# Revit family: Messblende 4000
name_source: partatom
category: Rohrzubehör
units: mm (PartAtom-declared; Revit-internal decimal feet)

## family parameters
Arbeitsebenenbasiert = Nein
Beim Laden mit Abzugskörper schneiden = Nein
Bemaßung runder Anschluss = Durchmesser verwenden
Gemeinsam genutzt = Nein
Immer vertikal = Ja
OmniClass-Nummer = 23.65.55.14
OmniClass-Titel = Valves for Liquid Services
Teiletyp = Unterbricht

## types (1)
- Messblende 4000
    Ausführung = Die Messblende aus entzinkungsbeständigem Messing besitzt zwei Messventile. Gemäß EN 10226 hat der Eingang ein Innengewinde Rp und der Ausgang ein Außengewinde R.
    Gehäuse = Messing, CC770S
    Hersteller = HERZ Armaturen Ges.m.b.H.
    Max. Betriebsdruck = 2000000.0 Pa
    Max. Betriebstemperatur (ab DN40) = 110 °C
    Max. Betriebstemperatur (bis DN32) = 130 °C
    Medium = Heizungswasserqualität nach ÖNORM H 5195 oder VDI-Richtline 2035.
Die Verwendung von Ethylen- oder Propylenglykol in einem Mischungsverhältnis 25 - 50 Vol.-% ist zulässig.
    Messventile = Messing, CW602N
    Min. Betriebstemperatur = -20 °C
    S03 = 10 mm  [stored 0.0328084 ft]
    SCRNCODE = 02;01;02
    SCRNSEQ = AWI;AWI_TYP="1001";02
    URL = www.herz-armaturen.at
    Verwendung = HERZ-Messblenden werden in die Strangleitungen von Warmwasser- Zentralheizungsanlagen sowie Kühlanlagen eingebaut und ermöglichen den hydraulischen Abgleich der Strangleitungen untereinander.
Der Einsatz der Messblenden ist im Vorlauf als auch im Rücklauf möglich.
Sie werden entweder eng gekoppelt an ein HERZ- Strangregulierventil installiert, um ein komplettes Set zu bilden oder in Verbindung mit einer HERZ Absperrarmatur eingesetzt.
Die Einregulierung des Stranges wird durch Einstellen des Strangregulierventiles während der Druckverlustmessung an der Messblende vorgenommen.
    Vorgabe-Ansicht = 0 mm  [stored 0 ft]

note: [stored X ft] marks values corroborated as IEEE doubles in the binary element streams (Revit-internal decimal feet)
